# Revit family: KingswayGroup_DrStps_Anti-LigatureDoorStopFloorMounted
name_source: partatom
category: Specialty Equipment
units: mm (PartAtom-declared; Revit-internal decimal feet)

## family parameters
Always vertical = Yes
Cut with Voids When Loaded = No
Part Type = Normal
Room Calculation Point = No
Round Connector Dimension = Use Diameter
Shared = No
Work Plane-Based = No

## types (1)
- KingswayGroup_DrStps_Anti-LigatureDoorStopFloorMounted
    AssetType = Fixed
    BIMObjectName = KingswayGroup_DoorStops_Anti-LigatureDoorStopFloorMounted
    Category = Pr_30_36_33_24:Door stops
    Color = For full range of available finishes and colours, contact Kingsway Group
    Default Elevation = 0 mm  [stored 0 ft]
    Description = Floor Mounted Door Stop
    DurationUnit = year
    Features = An anti-ligature floor mounted door stop manufactured from stainless steel with high impact rubber, designed to prevent doors and surfaces from damaging each other when the door is opened
    Finish = For full range of available finishes and colours, contact Kingsway Group
    IfcExportAs = IfcDiscreteAccessoryType
    IfcExportType = USERDEFINED
    Manufacturer = Kingsway Group
    ManufacturerName = Kingsway Group
    ManufacturerURL = https://kingswaygroupglobal.com
    Material = Stainless Steel, Rubber
    Model = KG181
    ModelNumber = KG181
    ModelReference = Anti-Ligature Door Stop Floor Mounted
    Name = DoorStops_Anti-LigatureDoorStopFloorMounted_KG181_KingswayGroup
    NominalHeight = 26 mm
    NominalLength = 45 mm  [stored 0.147638 ft]
    NominalWidth = 45 mm  [stored 0.147638 ft]
    PlateMaterial = NBS_Concept
    ProductInformation = https://kingswaygroupglobal.com
    RubberMaterial = NBS_Concept
    Size = 45 x 25.5 x 45 mm
    URL = https://kingswaygroupglobal.com
    Uniclass2015Code = Pr_30_36_33_24
    Uniclass2015Title = Door stops
    Uniclass2015Version = Products v1.36
    Version = 1
    WarrantyDescription = 5-Year Guarantee *For faulty manufacture and not for damage
    WarrantyDurationParts = 5
    WarrantyDurationUnit = year

note: [stored X ft] marks values corroborated as IEEE doubles in the binary element streams (Revit-internal decimal feet)

## geometry (parser evidence)
native form markers: Sweep x3
no freeform markers — native parametric forms only
